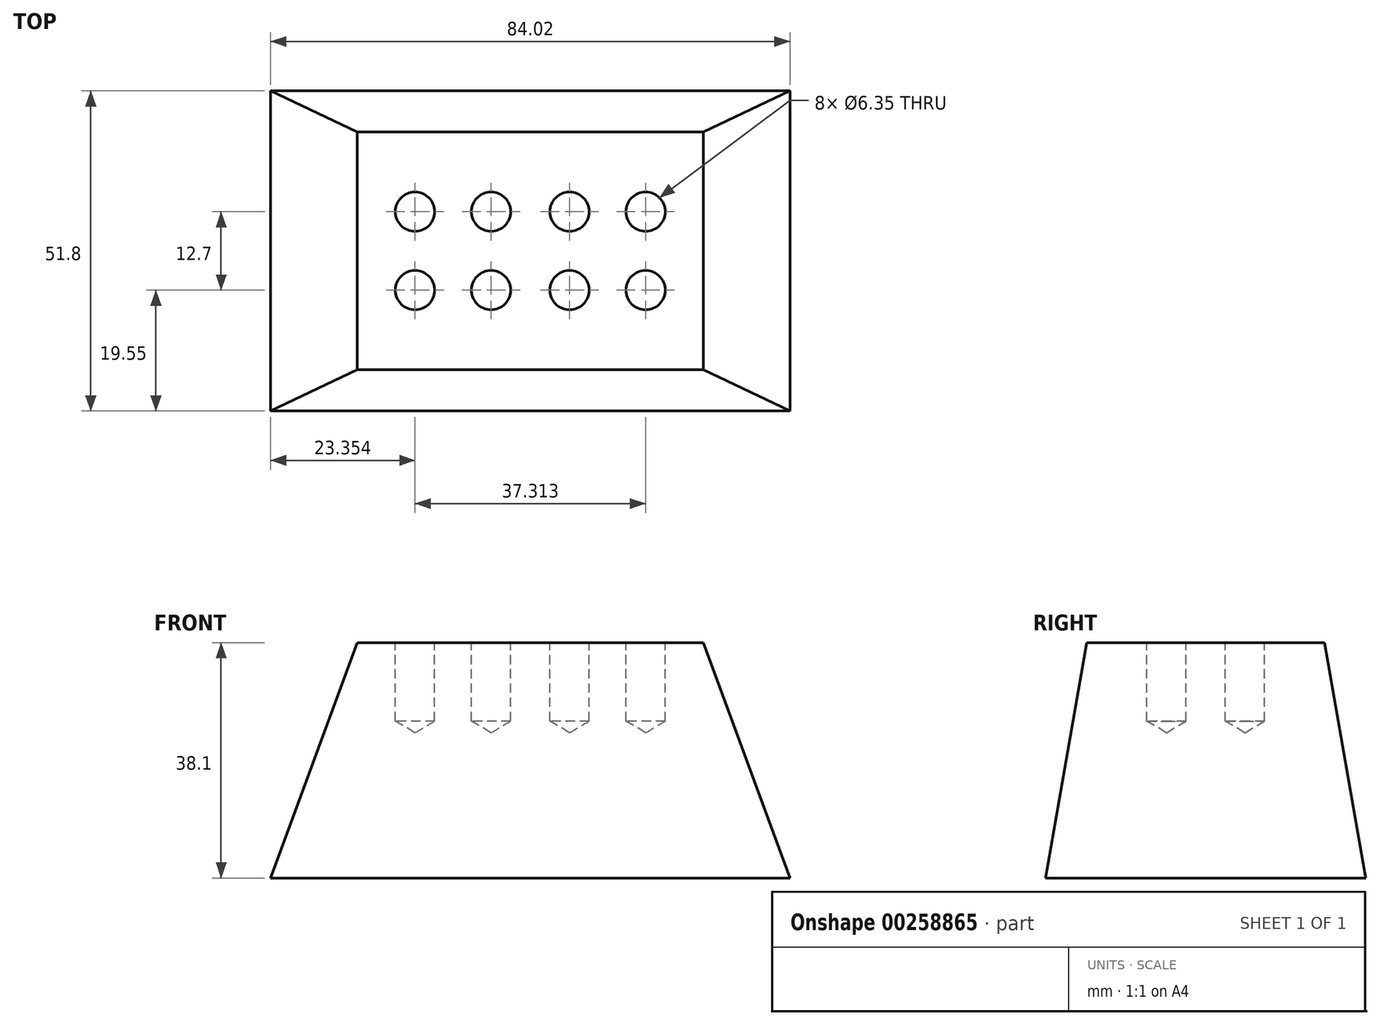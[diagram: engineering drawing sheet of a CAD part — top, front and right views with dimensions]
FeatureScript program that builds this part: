
annotation { "Feature Type Name" : "Feature", "Feature Type Description" : "" }
export const myFeature = defineFeature(function(context is Context, id is Id, definition is map)
    precondition{}
    {
        {
            var Q0;
            Q0=qCreatedBy(makeId("Top.planeOp"),FACE);
            var sketch = newSketch(context, id + "F0", { "sketchPlane" : qUnion([Q0])});
            skLineSegment(sketch, "E0.bottom", {"start": v(42.01, -25.9) * mm, "end": v(-42.01, -25.9) * mm});
            skLineSegment(sketch, "E0.top", {"start": v(42.01, 25.9) * mm, "end": v(-42.01, 25.9) * mm});
            skLineSegment(sketch, "E0.left", {"start": v(42.01, -25.9) * mm, "end": v(42.01, 25.9) * mm});
            skLineSegment(sketch, "E0.right", {"start": v(-42.01, -25.9) * mm, "end": v(-42.01, 25.9) * mm});
            skPoint(sketch, "E0.middle", {"position": v(0, 0) * mm});
            skSolve(sketch);
        }
        {
            var Q0;
            Q0=makeQuery(id+"F0.imprint","IMPRINT",FACE,{"disambiguationData":[TD([[makeQuery(id+"F0.imprint","IMPRINT",EDGE,{"derivedFrom":sQuery(id+"F0.wireOp",EDGE,"E0.bottom")}),-1.0]])]});
            cPlane(context, id + "F1", {"entities" : qUnion([Q0]), "cplaneType" : CPlaneType.OFFSET, "offset" : 38.1 * mm, "width" : 152.4 * mm, "height" : 152.4 * mm});
        }
        {
            var Q0;
            Q0=qCreatedBy(id+"F1.planeOp",FACE);
            var sketch = newSketch(context, id + "F2", { "sketchPlane" : qUnion([Q0])});
            skLineSegment(sketch, "E1.bottom", {"start": v(-28, 19.25) * mm, "end": v(28, 19.25) * mm});
            skLineSegment(sketch, "E1.top", {"start": v(-28, -19.25) * mm, "end": v(28, -19.25) * mm});
            skLineSegment(sketch, "E1.left", {"start": v(-28, 19.25) * mm, "end": v(-28, -19.25) * mm});
            skLineSegment(sketch, "E1.right", {"start": v(28, 19.25) * mm, "end": v(28, -19.25) * mm});
            skPoint(sketch, "E1.middle", {"position": v(0, 0) * mm});
            skSolve(sketch);
        }
        {
            var Q0;
            Q0=makeQuery(id+"F0.imprint","IMPRINT",FACE,{"disambiguationData":[TD([[makeQuery(id+"F0.imprint","IMPRINT",EDGE,{"derivedFrom":sQuery(id+"F0.wireOp",EDGE,"E0.bottom")}),-1.0]])]});
            var Q1;
            Q1=makeQuery(id+"F2.imprint","IMPRINT",FACE,{"disambiguationData":[TD([[makeQuery(id+"F2.imprint","IMPRINT",EDGE,{"derivedFrom":sQuery(id+"F2.wireOp",EDGE,"E1.bottom")}),-1.0]])]});
            loft(context, id + "F3", {"sheetProfilesArray" : [{ "sheetProfileEntities" : qUnion([Q0]) }, { "sheetProfileEntities" : qUnion([Q1]) }]});
        }
        {
            var Q0;
            Q0=makeQuery(id+"F2.imprint","IMPRINT",FACE,{"disambiguationData":[TD([[makeQuery(id+"F2.imprint","IMPRINT",EDGE,{"derivedFrom":sQuery(id+"F2.wireOp",EDGE,"E1.bottom")}),-1.0]])]});
            var sketch = newSketch(context, id + "F4", { "sketchPlane" : qUnion([Q0])});
            skPoint(sketch, "E2", {"position": v(-18.66, 6.35) * mm});
            skPoint(sketch, "E3", {"position": v(-6.35, 6.35) * mm});
            skPoint(sketch, "E4.MirrorP", {"position": v(6.35, 6.35) * mm});
            skPoint(sketch, "E5.MirrorP", {"position": v(18.66, 6.35) * mm});
            skPoint(sketch, "E6.MirrorP", {"position": v(-6.35, -6.35) * mm});
            skPoint(sketch, "E7.MirrorP", {"position": v(-18.66, -6.35) * mm});
            skPoint(sketch, "E8.MirrorP", {"position": v(6.35, -6.35) * mm});
            skPoint(sketch, "E9.MirrorP", {"position": v(18.66, -6.35) * mm});
            skSolve(sketch);
        }
        {
            var Q0;
            Q0=sQuery(id+"F4.wireOp",VERTEX,"E6.MirrorP");
            var Q1;
            Q1=sQuery(id+"F4.wireOp",VERTEX,"E3");
            var Q2;
            Q2=sQuery(id+"F4.wireOp",VERTEX,"E8.MirrorP");
            var Q3;
            Q3=sQuery(id+"F4.wireOp",VERTEX,"E2");
            var Q4;
            Q4=sQuery(id+"F4.wireOp",VERTEX,"E9.MirrorP");
            var Q5;
            Q5=sQuery(id+"F4.wireOp",VERTEX,"E7.MirrorP");
            var Q6;
            Q6=sQuery(id+"F4.wireOp",VERTEX,"E4.MirrorP");
            var Q7;
            Q7=sQuery(id+"F4.wireOp",VERTEX,"E5.MirrorP");
            var Q8;
            Q8=makeQuery(id+"F3.opLoft","SWEPT_BODY",BODY,{"disambiguationData":[OSD([makeQuery(id+"F0.imprint","IMPRINT",FACE,{"disambiguationData":[TD([[makeQuery(id+"F0.imprint","IMPRINT",EDGE,{"derivedFrom":sQuery(id+"F0.wireOp",EDGE,"E0.bottom")}),-1.0]])]}),makeQuery(id+"F2.imprint","IMPRINT",FACE,{"disambiguationData":[TD([[makeQuery(id+"F2.imprint","IMPRINT",EDGE,{"derivedFrom":sQuery(id+"F2.wireOp",EDGE,"E1.bottom")}),-1.0]])]})])]});
            hole(context, id + "F5", {"style" : HoleStyle.SIMPLE, "endStyle" : HoleEndStyle.BLIND, "holeDiameter" : 6.35 * mm, "holeDepth" : 12.7 * mm, "tappedDepth" : 12.7 * mm, "tapClearance" : 3, "locations" : qUnion([Q0, Q1, Q2, Q3, Q4, Q5, Q6, Q7]), "scope" : qUnion([Q8])});
        }
    });
